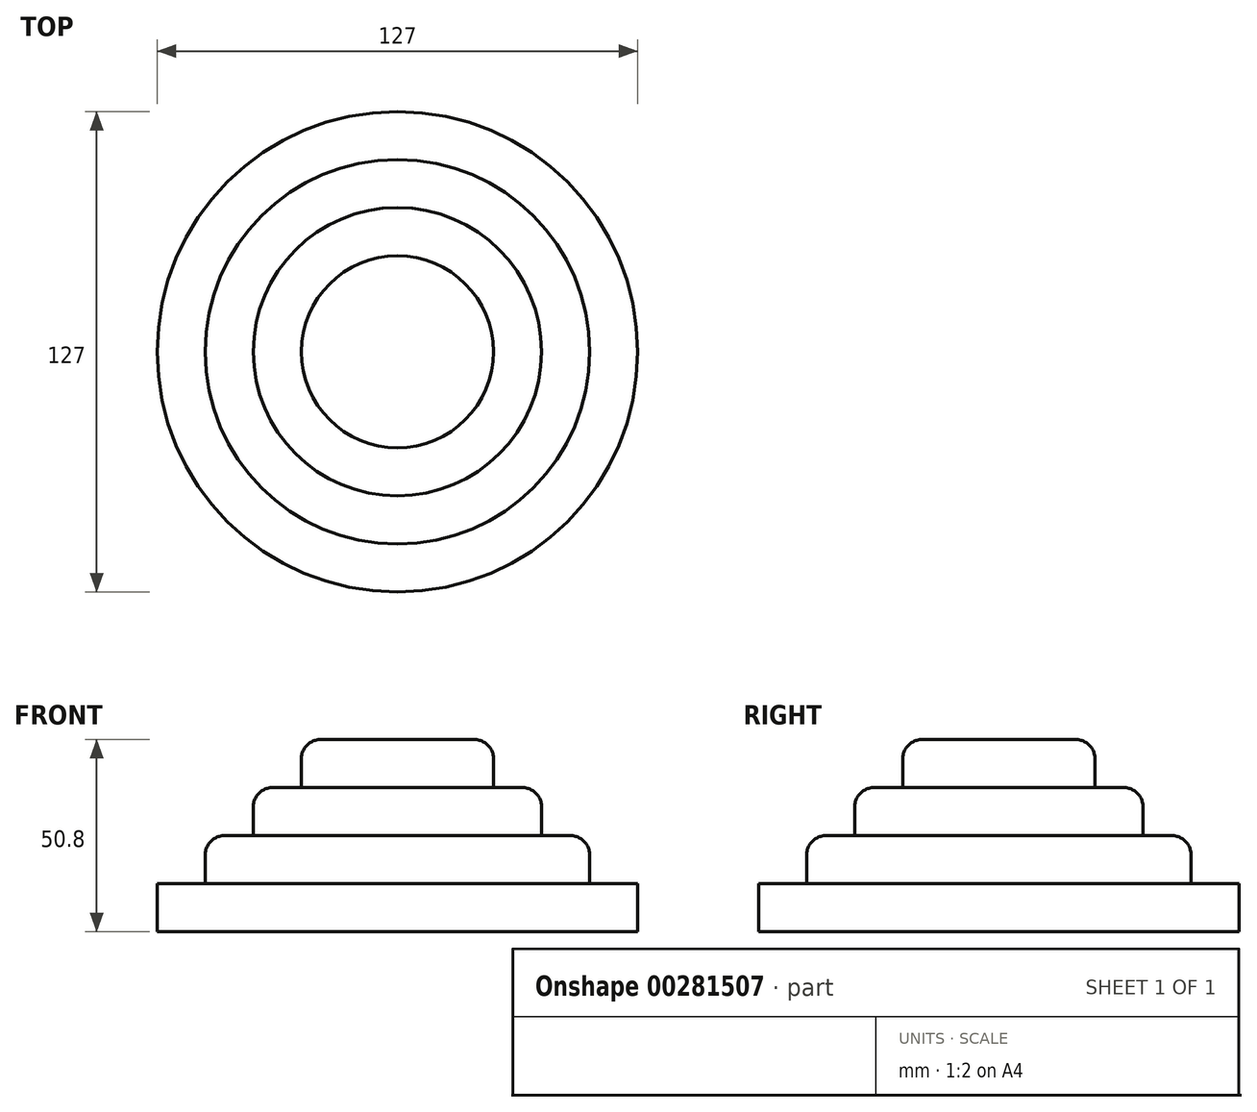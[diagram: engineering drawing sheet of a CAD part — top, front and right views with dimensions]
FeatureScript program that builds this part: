
annotation { "Feature Type Name" : "Feature", "Feature Type Description" : "" }
export const myFeature = defineFeature(function(context is Context, id is Id, definition is map)
    precondition{}
    {
        {
            var Q0;
            Q0=qCreatedBy(makeId("Top.planeOp"),FACE);
            var sketch = newSketch(context, id + "F0", { "sketchPlane" : qUnion([Q0])});
            skCircle(sketch, "E0", {"center": v(0, 0) * mm, "radius": 63.5 * mm});
            skSolve(sketch);
        }
        {
            var Q0;
            Q0=makeQuery(id+"F0.imprint","IMPRINT",FACE,{"disambiguationData":[TD([[makeQuery(id+"F0.imprint","IMPRINT",EDGE,{"derivedFrom":sQuery(id+"F0.wireOp",EDGE,"E0")}),1.0]])]});
            extrude(context, id + "F1", {"entities" : qUnion([Q0]), "depth" : 12.7 * mm});
        }
        {
            var Q0;
            Q0=qCreatedBy(makeId("Top.planeOp"),FACE);
            var sketch = newSketch(context, id + "F2", { "sketchPlane" : qUnion([Q0])});
            skCircle(sketch, "E1", {"center": v(0, 0) * mm, "radius": 12.7 * mm});
            skSolve(sketch);
        }
        {
            var Q0;
            Q0=sQuery(id+"F2.wireOp",EDGE,"E1");
            extrude(context, id + "F3", {"bodyType" : ToolBodyType.SURFACE, "operationType" : NewBodyOperationType.ADD, "surfaceEntities" : qUnion([Q0]), "depth" : 76.2 * mm});
        }
        {
            var Q0;
            Q0=qCreatedBy(makeId("Top.planeOp"),FACE);
            var sketch = newSketch(context, id + "F4", { "sketchPlane" : qUnion([Q0])});
            skCircle(sketch, "E2", {"center": v(0, 0) * mm, "radius": 50.8 * mm});
            skSolve(sketch);
        }
        {
            var Q0;
            Q0 = qSketchRegion(id + "F4", true);
            extrude(context, id + "F5", {"entities" : qUnion([Q0]), "operationType" : NewBodyOperationType.ADD, "depth" : 25.4 * mm});
        }
        {
            var Q0;
            Q0=qCreatedBy(makeId("Top.planeOp"),FACE);
            var sketch = newSketch(context, id + "F6", { "sketchPlane" : qUnion([Q0])});
            skCircle(sketch, "E3", {"center": v(0, 0) * mm, "radius": 38.1 * mm});
            skSolve(sketch);
        }
        {
            var Q0;
            Q0 = qSketchRegion(id + "F6", true);
            extrude(context, id + "F7", {"entities" : qUnion([Q0]), "operationType" : NewBodyOperationType.ADD, "depth" : 38.1 * mm});
        }
        {
            var Q0;
            Q0=qCreatedBy(makeId("Top.planeOp"),FACE);
            var sketch = newSketch(context, id + "F8", { "sketchPlane" : qUnion([Q0])});
            skCircle(sketch, "E4", {"center": v(0, 0) * mm, "radius": 25.4 * mm});
            skSolve(sketch);
        }
        {
            var Q0;
            Q0 = qSketchRegion(id + "F8", true);
            extrude(context, id + "F9", {"entities" : qUnion([Q0]), "operationType" : NewBodyOperationType.ADD, "depth" : 50.8 * mm});
        }
        {
            var Q0;
            Q0=makeQuery(id+"F9.opExtrude","CAP_EDGE",EDGE,{"disambiguationData":[OSD([sQuery(id+"F8.wireOp",EDGE,"E4")])],"isStart":false});
            fillet(context, id + "F10", {"entities" : qUnion([Q0]), "radius" : 5.08 * mm, "tangentPropagation" : true, "allowEdgeOverflow" : false});
        }
        {
            var Q0;
            Q0=makeQuery(id+"F7.opExtrude","CAP_EDGE",EDGE,{"disambiguationData":[OSD([sQuery(id+"F6.wireOp",EDGE,"E3")])],"isStart":false});
            fillet(context, id + "F11", {"entities" : qUnion([Q0]), "radius" : 5.08 * mm, "tangentPropagation" : true, "allowEdgeOverflow" : false});
        }
        {
            var Q0;
            Q0=makeQuery(id+"F5.opExtrude","CAP_EDGE",EDGE,{"disambiguationData":[OSD([sQuery(id+"F4.wireOp",EDGE,"E2")])],"isStart":false});
            fillet(context, id + "F12", {"entities" : qUnion([Q0]), "radius" : 5.08 * mm, "tangentPropagation" : true, "allowEdgeOverflow" : false});
        }
    });
